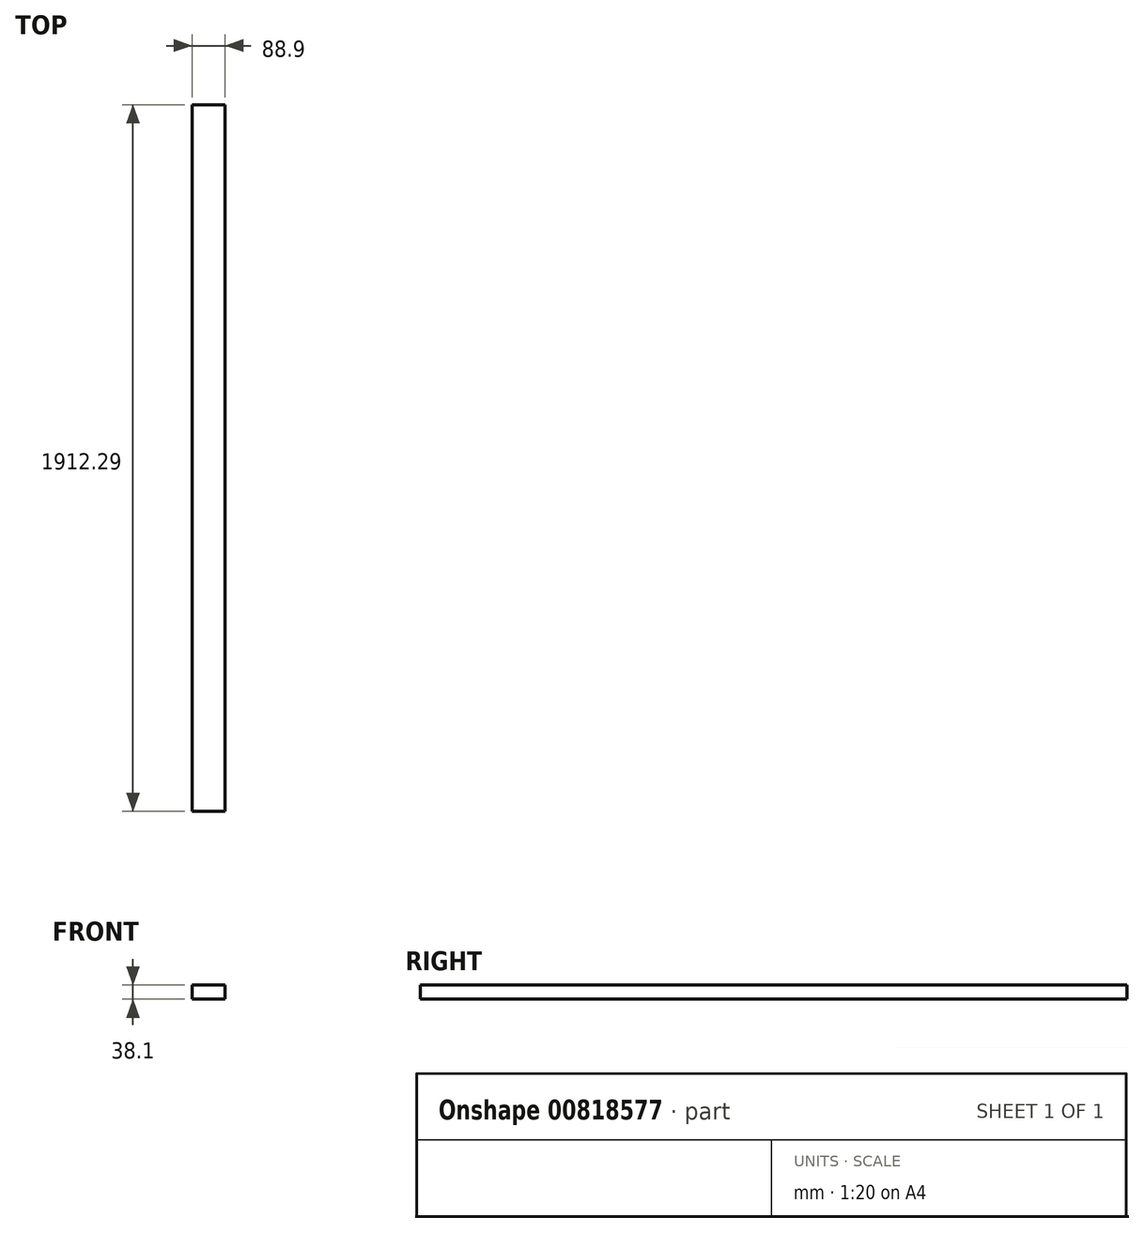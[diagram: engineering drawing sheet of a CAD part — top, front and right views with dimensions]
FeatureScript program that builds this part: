
annotation { "Feature Type Name" : "Feature", "Feature Type Description" : "" }
export const myFeature = defineFeature(function(context is Context, id is Id, definition is map)
    precondition{}
    {
        {
            var Q0;
            Q0=qCreatedBy(makeId("Front.planeOp"),FACE);
            var sketch = newSketch(context, id + "F0", { "sketchPlane" : qUnion([Q0])});
            skLineSegment(sketch, "E0.bottom", {"start": v(-45.55, 13.98) * mm, "end": v(43.35, 13.98) * mm});
            skLineSegment(sketch, "E0.top", {"start": v(-45.55, -24.12) * mm, "end": v(43.35, -24.12) * mm});
            skLineSegment(sketch, "E0.left", {"start": v(-45.55, 13.98) * mm, "end": v(-45.55, -24.12) * mm});
            skLineSegment(sketch, "E0.right", {"start": v(43.35, 13.98) * mm, "end": v(43.35, -24.12) * mm});
            skSolve(sketch);
        }
        {
            var Q0;
            Q0 = qSketchRegion(id + "F0", true);
            extrude(context, id + "F1", {"entities" : qUnion([Q0]), "depth" : 1912.3 * mm, "offsetDistance" : 25.4 * mm});
        }
    });
